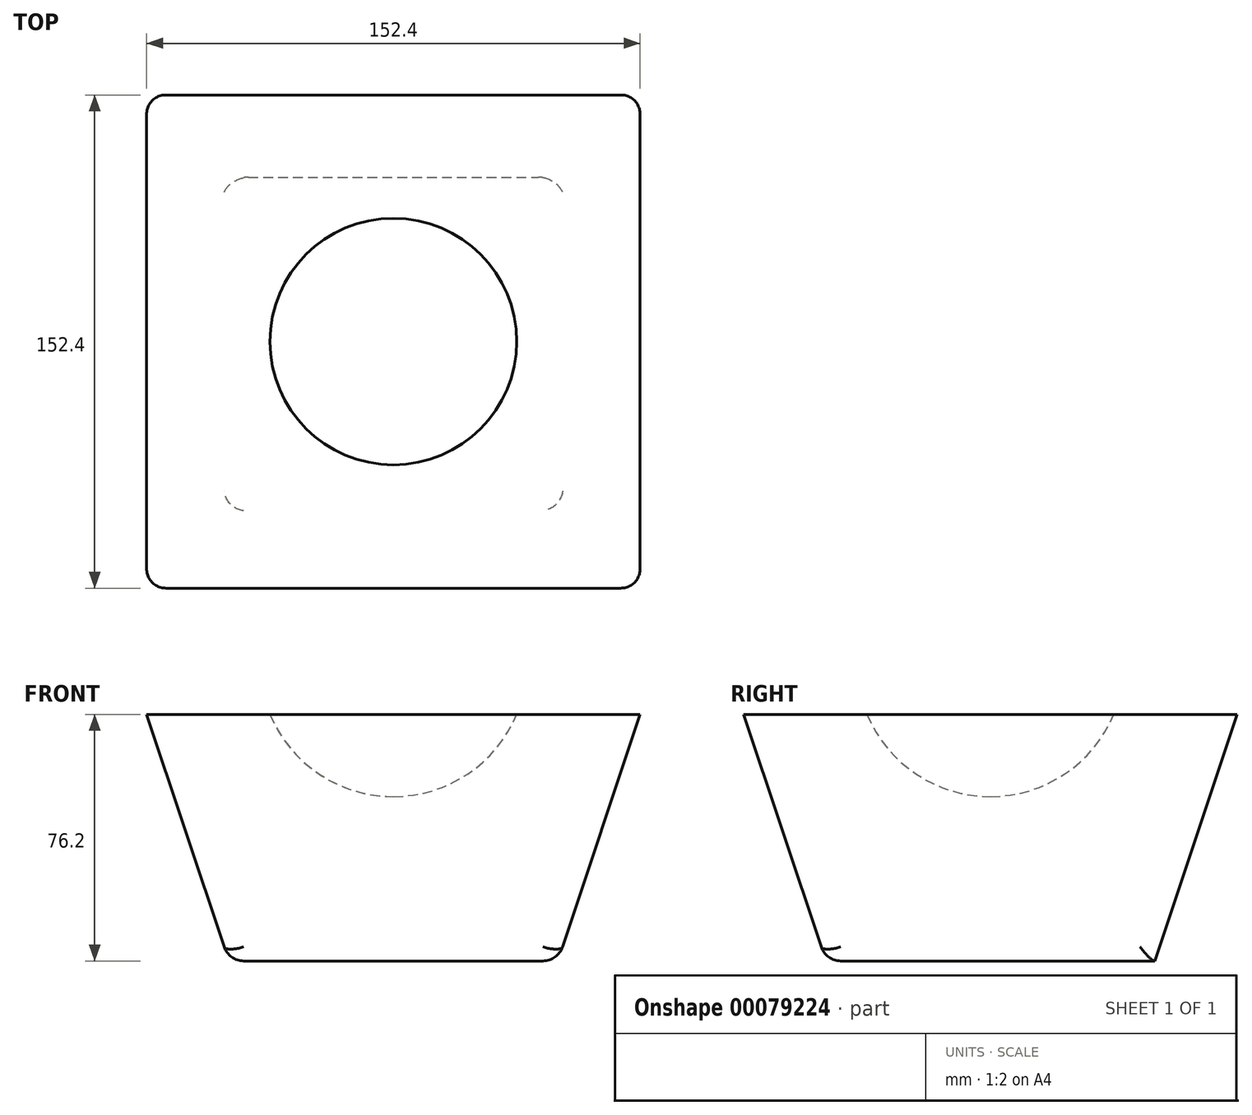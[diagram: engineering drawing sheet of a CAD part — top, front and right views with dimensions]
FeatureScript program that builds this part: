
annotation { "Feature Type Name" : "Feature", "Feature Type Description" : "" }
export const myFeature = defineFeature(function(context is Context, id is Id, definition is map)
    precondition{}
    {
        {
            var Q0;
            Q0=qCreatedBy(makeId("Top.planeOp"),FACE);
            var sketch = newSketch(context, id + "F0", { "sketchPlane" : qUnion([Q0])});
            skLineSegment(sketch, "E0.bottom", {"start": v(-50.8, 50.8) * mm, "end": v(50.8, 50.8) * mm});
            skLineSegment(sketch, "E0.top", {"start": v(-50.8, -50.8) * mm, "end": v(50.8, -50.8) * mm});
            skLineSegment(sketch, "E0.left", {"start": v(-50.8, 50.8) * mm, "end": v(-50.8, -50.8) * mm});
            skLineSegment(sketch, "E0.right", {"start": v(50.8, 50.8) * mm, "end": v(50.8, -50.8) * mm});
            skLineSegment(sketch, "E1.bottom", {"start": v(-76.2, 76.2) * mm, "end": v(76.2, 76.2) * mm, "construction": true});
            skLineSegment(sketch, "E1.top", {"start": v(-76.2, -76.2) * mm, "end": v(76.2, -76.2) * mm, "construction": true});
            skLineSegment(sketch, "E1.left", {"start": v(-76.2, 76.2) * mm, "end": v(-76.2, -76.2) * mm, "construction": true});
            skLineSegment(sketch, "E1.right", {"start": v(76.2, 76.2) * mm, "end": v(76.2, -76.2) * mm, "construction": true});
            skSolve(sketch);
        }
        {
            var Q0;
            Q0=qCreatedBy(makeId("Top.planeOp"),FACE);
            cPlane(context, id + "F1", {"entities" : qUnion([Q0]), "cplaneType" : CPlaneType.OFFSET, "offset" : 76.2 * mm, "width" : 152.4 * mm, "height" : 152.4 * mm});
        }
        {
            var Q0;
            Q0=qCreatedBy(id+"F1.planeOp",FACE);
            var sketch = newSketch(context, id + "F2", { "sketchPlane" : qUnion([Q0])});
            skLineSegment(sketch, "E2.0", {"start": v(-76.2, 76.2) * mm, "end": v(-76.2, -76.2) * mm});
            skLineSegment(sketch, "E2.1", {"start": v(-76.2, -76.2) * mm, "end": v(76.2, -76.2) * mm});
            skLineSegment(sketch, "E2.2", {"start": v(-76.2, 76.2) * mm, "end": v(76.2, 76.2) * mm});
            skLineSegment(sketch, "E2.3", {"start": v(76.2, 76.2) * mm, "end": v(76.2, -76.2) * mm});
            skSolve(sketch);
        }
        {
            var Q0;
            Q0=makeQuery(id+"F0.imprint","IMPRINT",FACE,{"disambiguationData":[TD([[makeQuery(id+"F0.imprint","IMPRINT",EDGE,{"derivedFrom":sQuery(id+"F0.wireOp",EDGE,"E0.bottom")}),-1.0]])]});
            var Q1;
            Q1=makeQuery(id+"F2.imprint","IMPRINT",FACE,{"disambiguationData":[TD([[makeQuery(id+"F2.imprint","IMPRINT",EDGE,{"derivedFrom":sQuery(id+"F2.wireOp",EDGE,"E2.0")}),1.0]])]});
            loft(context, id + "F3", {"sheetProfilesArray" : [{ "sheetProfileEntities" : qUnion([Q0]) }, { "sheetProfileEntities" : qUnion([Q1]) }]});
        }
        {
            var Q0;
            Q0=qCreatedBy(makeId("Front.planeOp"),FACE);
            var sketch = newSketch(context, id + "F4", { "sketchPlane" : qUnion([Q0])});
            skLineSegment(sketch, "E3", {"start": v(0, 76.2) * mm, "end": v(38.1, 76.2) * mm});
            skLineSegment(sketch, "E4", {"start": v(0, 76.2) * mm, "end": v(-38.1, 76.2) * mm});
            skLineSegment(sketch, "E5", {"start": v(0, 76.2) * mm, "end": v(0, 50.8) * mm});
            skCircle(sketch, "E6", {"center": v(0, 92.07) * mm, "radius": 41.27 * mm});
            skSolve(sketch);
        }
        {
            var Q0;
            {var subQ0=sQuery(id+"F4.wireOp",EDGE,"E4");Q0=makeQuery(id+"F4.imprint","IMPRINT",FACE,{"disambiguationData":[TD([[makeQuery(id+"F4.imprint","IMPRINT",EDGE,{"derivedFrom":subQ0}),1.0]])]});}
            var Q1;
            Q1=sQuery(id+"F4.wireOp",EDGE,"E5");
            revolve(context, id + "F5", {"operationType" : NewBodyOperationType.REMOVE, "entities" : qUnion([Q0]), "axis" : qUnion([Q1]), "revolveType" : RevolveType.FULL, "oppositeDirection" : true});
        }
        {
            var Q0;
            Q0=makeQuery(id+"F3.opLoft","SWEPT_EDGE",EDGE,{"disambiguationData":[OSD([sQuery(id+"F0.wireOp",EDGE,"E0.top"),sQuery(id+"F0.wireOp",EDGE,"E0.right"),sQuery(id+"F2.wireOp",EDGE,"E2.1"),sQuery(id+"F2.wireOp",EDGE,"E2.3")])]});
            var Q1;
            Q1=makeQuery(id+"F3.opLoft","SWEPT_EDGE",EDGE,{"disambiguationData":[OSD([sQuery(id+"F0.wireOp",EDGE,"E0.top"),sQuery(id+"F0.wireOp",EDGE,"E0.left"),sQuery(id+"F2.wireOp",EDGE,"E2.0"),sQuery(id+"F2.wireOp",EDGE,"E2.1")])]});
            var Q2;
            Q2=makeQuery(id+"F3.opLoft","MID_CAP_EDGE",EDGE,{"disambiguationData":[OSD([sQuery(id+"F0.wireOp",EDGE,"E0.top"),sQuery(id+"F0.wireOp",EDGE,"E0.left"),sQuery(id+"F0.wireOp",EDGE,"E0.right")])],"capPos":0.0});
            var Q3;
            Q3=makeQuery(id+"F3.opLoft","MID_CAP_EDGE",EDGE,{"disambiguationData":[OSD([sQuery(id+"F0.wireOp",EDGE,"E0.bottom"),sQuery(id+"F0.wireOp",EDGE,"E0.top"),sQuery(id+"F0.wireOp",EDGE,"E0.right")])],"capPos":0.0});
            var Q4;
            Q4=makeQuery(id+"F3.opLoft","SWEPT_EDGE",EDGE,{"disambiguationData":[OSD([sQuery(id+"F0.wireOp",EDGE,"E0.bottom"),sQuery(id+"F0.wireOp",EDGE,"E0.right"),sQuery(id+"F2.wireOp",EDGE,"E2.2"),sQuery(id+"F2.wireOp",EDGE,"E2.3")])]});
            var Q5;
            Q5=makeQuery(id+"F3.opLoft","SWEPT_EDGE",EDGE,{"disambiguationData":[OSD([sQuery(id+"F0.wireOp",EDGE,"E0.bottom"),sQuery(id+"F0.wireOp",EDGE,"E0.left"),sQuery(id+"F2.wireOp",EDGE,"E2.0"),sQuery(id+"F2.wireOp",EDGE,"E2.2")])]});
            var Q6;
            Q6=makeQuery(id+"F3.opLoft","MID_CAP_EDGE",EDGE,{"disambiguationData":[OSD([sQuery(id+"F0.wireOp",EDGE,"E0.bottom"),sQuery(id+"F0.wireOp",EDGE,"E0.top"),sQuery(id+"F0.wireOp",EDGE,"E0.left")])],"capPos":0.0});
            fillet(context, id + "F6", {"entities" : qUnion([Q0, Q1, Q2, Q3, Q4, Q5, Q6]), "radius" : 6.35 * mm, "tangentPropagation" : true, "allowEdgeOverflow" : false});
        }
    });
